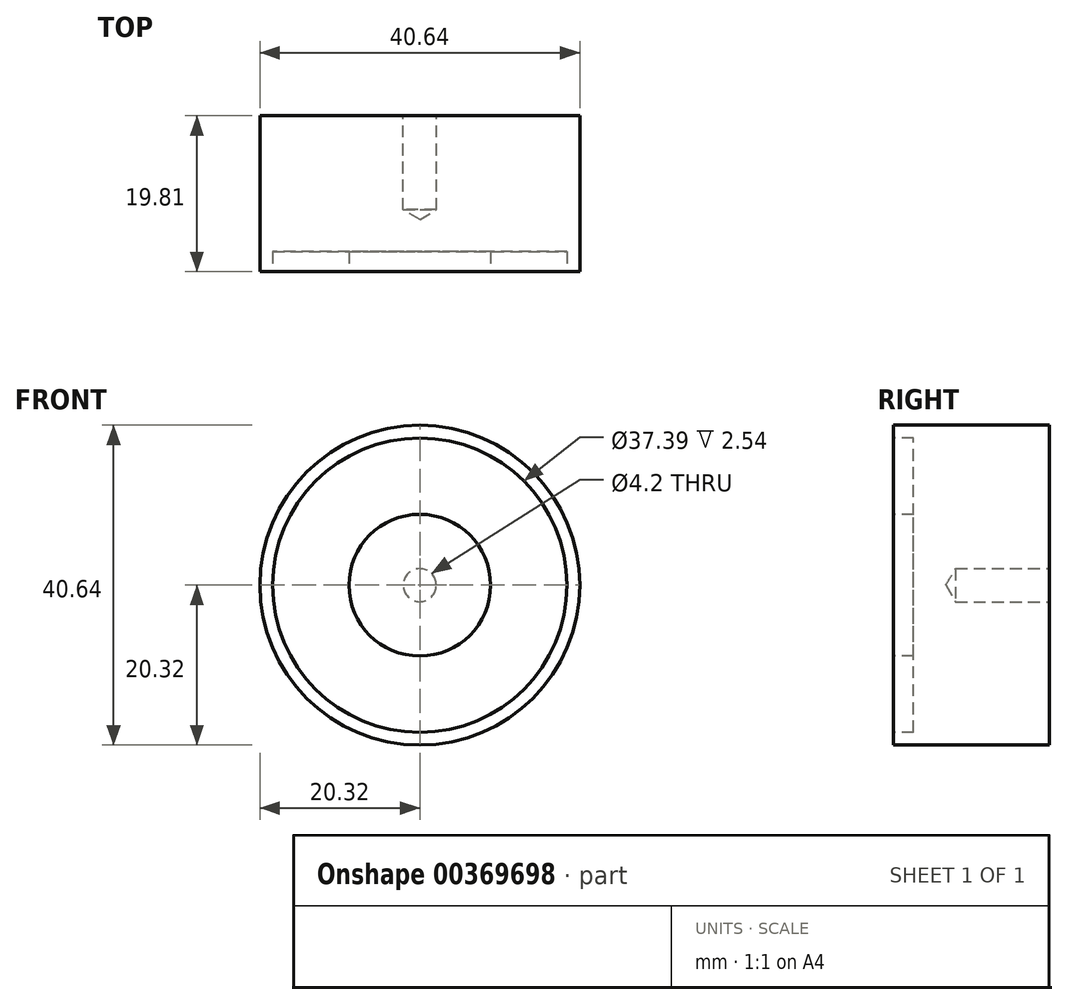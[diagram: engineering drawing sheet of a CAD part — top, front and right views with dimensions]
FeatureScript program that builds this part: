
annotation { "Feature Type Name" : "Feature", "Feature Type Description" : "" }
export const myFeature = defineFeature(function(context is Context, id is Id, definition is map)
    precondition{}
    {
        {
            var Q0;
            Q0=qCreatedBy(makeId("Front.planeOp"),FACE);
            var sketch = newSketch(context, id + "F0", { "sketchPlane" : qUnion([Q0])});
            skCircle(sketch, "E0", {"center": v(0, 0) * mm, "radius": 20.32 * mm});
            skSolve(sketch);
        }
        {
            var Q0;
            Q0 = qSketchRegion(id + "F0", true);
            extrude(context, id + "F1", {"entities" : qUnion([Q0]), "depth" : 19.8 * mm, "offsetDistance" : 25.4 * mm});
        }
        {
            var Q0;
            Q0=makeQuery(id+"F1.opExtrude","CAP_FACE",FACE,{"disambiguationData":[OSD([sQuery(id+"F0.wireOp",EDGE,"E0")])],"isStart":false});
            var sketch = newSketch(context, id + "F2", { "sketchPlane" : qUnion([Q0])});
            skCircle(sketch, "E1", {"center": v(0, 0) * mm, "radius": 18.7 * mm});
            skCircle(sketch, "E2", {"center": v(0, 0) * mm, "radius": 9 * mm});
            skSolve(sketch);
        }
        {
            var Q0;
            Q0 = qSketchRegion(id + "F2", true);
            extrude(context, id + "F3", {"entities" : qUnion([Q0]), "operationType" : NewBodyOperationType.REMOVE, "oppositeDirection" : true, "depth" : 2.54 * mm, "offsetDistance" : 25.4 * mm});
        }
        {
            var Q0;
            Q0=makeQuery(id+"F1.opExtrude","CAP_FACE",FACE,{"disambiguationData":[OSD([sQuery(id+"F0.wireOp",EDGE,"E0")])],"isStart":true});
            var sketch = newSketch(context, id + "F4", { "sketchPlane" : qUnion([Q0])});
            skPoint(sketch, "E3", {"position": v(0, 0) * mm});
            skSolve(sketch);
        }
        {
            var Q0;
            Q0=sQuery(id+"F4.wireOp",VERTEX,"E3");
            var Q1;
            Q1=makeQuery(id+"F1.opExtrude","SWEPT_BODY",BODY,{"disambiguationData":[OSD([sQuery(id+"F0.wireOp",EDGE,"E0")])]});
            hole(context, id + "F5", {"style" : HoleStyle.SIMPLE, "endStyle" : HoleEndStyle.BLIND, "standardTappedOrClearance" : lookupTablePath({ "standard" : "ISO", "engagement" : "75%", "pitch" : "0.8 mm", "size" : "M5", "type" : "Tapped" }), "standardBlindInLast" : lookupTablePath({ "standard" : "ISO", "engagement" : "75%", "pitch" : "0.8 mm", "size" : "M5", "type" : "Tapped" }), "holeDiameter" : 4.2 * mm, "showTappedDepth" : true, "holeDepth" : 11.92 * mm, "tappedDepth" : 9.52 * mm, "tapClearance" : 3, "startFromSketch" : true, "locations" : qUnion([Q0]), "scope" : qUnion([Q1]), "majorDiameter" : 5 * mm});
        }
    });
